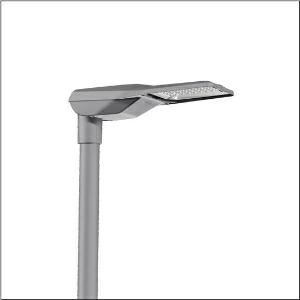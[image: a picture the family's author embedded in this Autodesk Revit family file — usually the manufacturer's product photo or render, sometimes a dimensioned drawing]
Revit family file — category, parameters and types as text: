
# Revit family: streetlight_sl_21_iq_mini___st0_8a_5xe2c41g08gb_95af
name_source: partatom
category: Lighting Fixtures
units: mm (PartAtom-declared; Revit-internal decimal feet)

## family parameters
Cut with Voids When Loaded = No
Host = Face
Light Source = No
Part Type = Normal
Room Calculation Point = No
Round Connector Dimension = Use Diameter
Shared = No

## types (1)
- --- (1 x LED, 5920 lm, 37.1 W, 4000K)
    Apparent Load = 37 VA
    CIE Flux Codes = 38 75 97 100 100
    Color Rendering = 70
    Color Temperature = 4000K
    Default Elevation = 1800 mm
    Description = Streetlight SL 21 iQ mini, mast luminaire, primary light control with lens, of PMMA, primary optical cover: cover, of toughened safety glass, transparent, light distribution: ST0.8a, light emission: direct distribution, primary light characteristic: asymmetric, installation type: post-top, side-entry, LED, High Power LED, rated luminous flux: 5.920lm, luminous efficacy: 160lm/W, light colour: 740, colour temperature: 4000K, control: Street-Remote, Auto-Match, Temp-Guard, Lumen-Switch, Night-Set, Smart-Wire, Light-Fading, Desk-Remote (wireless, voltage-free reading and setting of iQ features in the workshop via application-optimized NFC function/RFID function), optimised constant luminous flux control (CLO 2.0), presetting dimming linear, mains connection: 220..240V, AC, 50/60Hz, start of lifetime: 37W, end of service life: 39W, reduction: 18W, luminaire housing, of diecast aluminium, powder-coated, Siteco® metallic grey (DB 702S), corrosivity category C5 mid according to DIN EN ISO 12944, please order mast flange separately, inclination adjustable: 0°, 5°, 10°, 15°, sealing non-destructively replaceable, multi-level sealing system, length: 628mm, width: 235mm, height: 110mm, mast flange for spigot size: 42mm (side-entry): 5XC10008XM4, 60/48mm (side-entry/post-top): 5XC10108XM2, 76/60mm (side-entry/post-top): 5XC10108XM1, protection rating (complete): IP66, insulation class (complete): insulation class II (safety insulation), certification: CE, ENEC, ENEC+, VDE, impact resistance: IK09, permissible operating ambient temperature for outdoor applications: -40..+50°C, standard-compliant lighting for roads and squares, packaging unit: 1 piece

Light Distribution: ST0.8a
    Height = 110 mm
    Lamp = 1 x LED
    Lamp Light Flux = 5920 lm
    Lamp Power = 37.1 W
    Lamp count = 1
    Length = 625 mm
    Luminous efficacy = 160 lm/W
    Manufacturer = Siteco
    ModVariant = No
    Model = 5XE2C41G08GB
    Number of Poles = 1
    OnlyDefault = Yes
    Power Factor = 1
    Product Name = Streetlight SL 21 iQ mini | ST0.8a
    Product group = mast luminaire | pylon top
    ProductGroupID = 6100
    Protection Class = Protection class II
    Protection Degree = IP 66
    RLX_Detail_Level = 1
    RLX_Emergency_Light_Flux = 0 lm
    RLX_Emergency_Type = 0
    RLX_Emergency_Type_DB = No
    RlxData = <blob elided: 92877 chars, md5=e64517b7>
    Socket = socket
    Standby Power = 0 W
    System Light Flux = 5920 lm
    System Power = 37 W
    Type Comments = factory setting: luminous flux: 100 % | dim-lin: 254 | 385 mA
    Type Image = l_1003519.jpg
    URL = http://relux.com
    VarID = @adj_118873
    Voltage = 0 V
    Weight = 0.00 kg
    Width = 234 mm

## geometry (parser evidence)
native form markers: Blend x4, Sweep x11
no freeform markers — native parametric forms only
